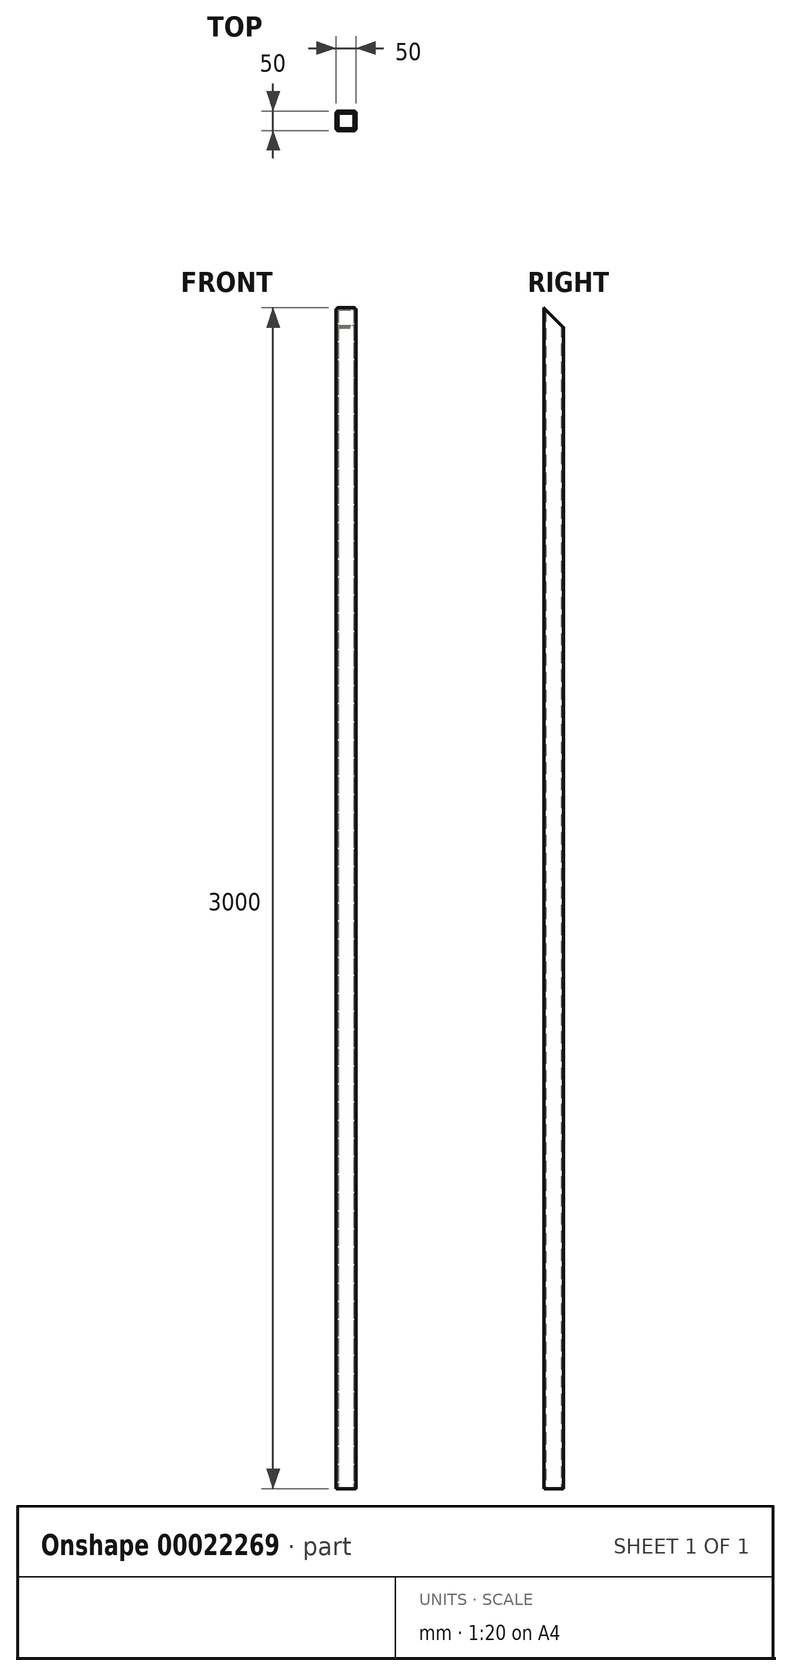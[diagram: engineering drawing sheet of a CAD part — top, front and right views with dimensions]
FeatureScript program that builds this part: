
annotation { "Feature Type Name" : "Feature", "Feature Type Description" : "" }
export const myFeature = defineFeature(function(context is Context, id is Id, definition is map)
    precondition{}
    {
        {
            var Q0;
            Q0=qCreatedBy(makeId("Top.planeOp"),FACE);
            var sketch = newSketch(context, id + "F0", { "sketchPlane" : qUnion([Q0])});
            skLineSegment(sketch, "E0.rect.bottom", {"start": v(20, 25) * mm, "end": v(-20, 25) * mm});
            skLineSegment(sketch, "E0.rect.top", {"start": v(20, -25) * mm, "end": v(-20, -25) * mm});
            skLineSegment(sketch, "E0.rect.left", {"start": v(25, 20) * mm, "end": v(25, -20) * mm});
            skLineSegment(sketch, "E0.rect.right", {"start": v(-25, 20) * mm, "end": v(-25, -20) * mm});
            skPoint(sketch, "E0.rect.middle", {"position": v(0, 0) * mm});
            skPoint(sketch, "E1.visualSharp", {"position": v(25, 25) * mm});
            skArc(sketch, "E1.filletArc", {"start": v(25, 20) * mm, "mid": v(23.54, 23.54) * mm, "end": v(20, 25) * mm});
            skPoint(sketch, "E2.visualSharp", {"position": v(-25, -25) * mm});
            skArc(sketch, "E2.filletArc", {"start": v(-25, -20) * mm, "mid": v(-23.54, -23.54) * mm, "end": v(-20, -25) * mm});
            skPoint(sketch, "E3.visualSharp", {"position": v(25, -25) * mm});
            skArc(sketch, "E3.filletArc", {"start": v(20, -25) * mm, "mid": v(23.54, -23.54) * mm, "end": v(25, -20) * mm});
            skPoint(sketch, "E4.visualSharp", {"position": v(-25, 25) * mm});
            skArc(sketch, "E4.filletArc", {"start": v(-20, 25) * mm, "mid": v(-23.54, 23.54) * mm, "end": v(-25, 20) * mm});
            skLineSegment(sketch, "E5.0", {"start": v(20, 17.5) * mm, "end": v(20, -17.5) * mm});
            skLineSegment(sketch, "E6.0", {"start": v(17.5, 20) * mm, "end": v(-17.5, 20) * mm});
            skLineSegment(sketch, "E7.0", {"start": v(17.5, -20) * mm, "end": v(-17.5, -20) * mm});
            skLineSegment(sketch, "E8.0", {"start": v(-20, 17.5) * mm, "end": v(-20, -17.5) * mm});
            skArc(sketch, "E9.filletArc", {"start": v(-17.5, 20) * mm, "mid": v(-19.27, 19.27) * mm, "end": v(-20, 17.5) * mm});
            skArc(sketch, "E10.filletArc", {"start": v(20, 17.5) * mm, "mid": v(19.27, 19.27) * mm, "end": v(17.5, 20) * mm});
            skArc(sketch, "E11.filletArc", {"start": v(17.5, -20) * mm, "mid": v(19.27, -19.27) * mm, "end": v(20, -17.5) * mm});
            skArc(sketch, "E12.filletArc", {"start": v(-20, -17.5) * mm, "mid": v(-19.27, -19.27) * mm, "end": v(-17.5, -20) * mm});
            skSolve(sketch);
        }
        {
            var Q0;
            Q0=makeQuery(id+"F0.imprint","IMPRINT",FACE,{"disambiguationData":[TD([[makeQuery(id+"F0.imprint","IMPRINT",EDGE,{"derivedFrom":sQuery(id+"F0.wireOp",EDGE,"E0.rect.bottom")}),1.0]])]});
            extrude(context, id + "F1", {"entities" : qUnion([Q0]), "depth" : 3000 * mm});
        }
        {
            var Q0;
            Q0=qCreatedBy(makeId("Right.planeOp"),FACE);
            var sketch = newSketch(context, id + "F2", { "sketchPlane" : qUnion([Q0])});
            skLineSegment(sketch, "E13", {"start": v(-25, 3000) * mm, "end": v(25, 2950) * mm});
            skLineSegment(sketch, "E14", {"start": v(25, 2950) * mm, "end": v(25, 3000) * mm});
            skLineSegment(sketch, "E15", {"start": v(25, 3000) * mm, "end": v(-25, 3000) * mm});
            skSolve(sketch);
        }
        {
            var Q0;
            Q0 = qSketchRegion(id + "F2", true);
            extrude(context, id + "F3", {"entities" : qUnion([Q0]), "operationType" : NewBodyOperationType.REMOVE, "oppositeDirection" : true, "depth" : 25 * mm, "hasSecondDirection" : true, "secondDirectionOppositeDirection" : false, "secondDirectionDepth" : 25 * mm});
        }
    });
